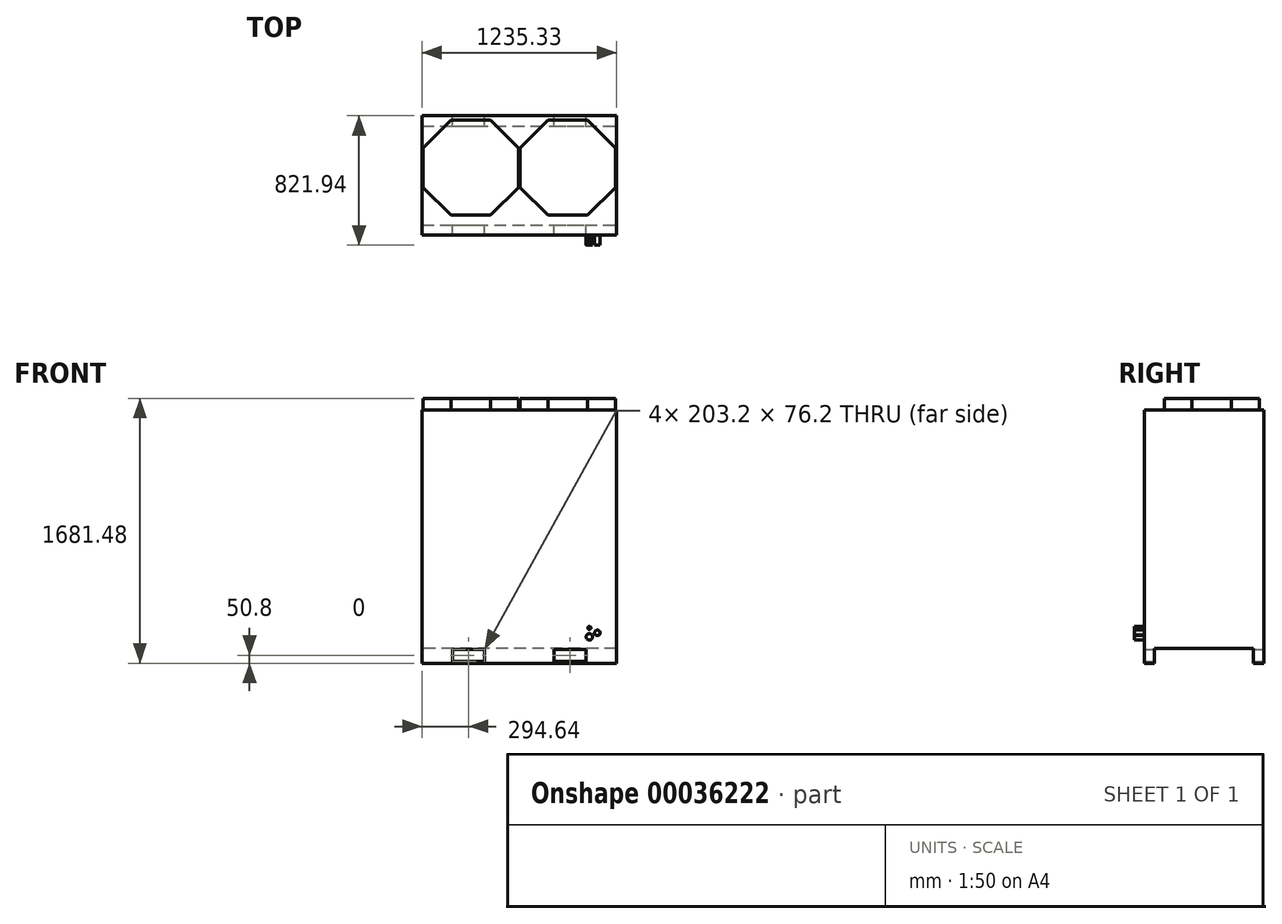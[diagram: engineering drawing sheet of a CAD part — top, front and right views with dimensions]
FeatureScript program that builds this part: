
annotation { "Feature Type Name" : "Feature", "Feature Type Description" : "" }
export const myFeature = defineFeature(function(context is Context, id is Id, definition is map)
    precondition{}
    {
        {
            var Q0;
            Q0=qCreatedBy(makeId("Front.planeOp"),FACE);
            var sketch = newSketch(context, id + "F0", { "sketchPlane" : qUnion([Q0])});
            skLineSegment(sketch, "E0.bottom", {"start": v(0, 0) * mm, "end": v(1235.33, 0) * mm});
            skLineSegment(sketch, "E0.top", {"start": v(0, 1610.36) * mm, "end": v(1235.33, 1610.36) * mm});
            skLineSegment(sketch, "E0.left", {"start": v(0, 0) * mm, "end": v(0, 1610.36) * mm});
            skLineSegment(sketch, "E0.right", {"start": v(1235.33, 0) * mm, "end": v(1235.33, 1610.36) * mm});
            skLineSegment(sketch, "E1.bottom", {"start": v(193.04, 88.9) * mm, "end": v(396.24, 88.9) * mm});
            skLineSegment(sketch, "E1.top", {"start": v(193.04, 12.7) * mm, "end": v(396.24, 12.7) * mm});
            skLineSegment(sketch, "E1.left", {"start": v(193.04, 88.9) * mm, "end": v(193.04, 12.7) * mm});
            skLineSegment(sketch, "E1.right", {"start": v(396.24, 88.9) * mm, "end": v(396.24, 12.7) * mm});
            skLineSegment(sketch, "E2.bottom", {"start": v(839.09, 88.9) * mm, "end": v(1042.29, 88.9) * mm});
            skLineSegment(sketch, "E2.top", {"start": v(839.09, 12.7) * mm, "end": v(1042.29, 12.7) * mm});
            skLineSegment(sketch, "E2.left", {"start": v(839.09, 88.9) * mm, "end": v(839.09, 12.7) * mm});
            skLineSegment(sketch, "E2.right", {"start": v(1042.29, 88.9) * mm, "end": v(1042.29, 12.7) * mm});
            skSolve(sketch);
        }
        {
            var Q0;
            Q0=qSketchRegion(id+"F0",true);
            extrude(context, id + "F1", {"entities" : qUnion([Q0]), "depth" : 758.44 * mm});
        }
        {
            var Q0;
            Q0=makeQuery(id+"F1.opExtrude","SWEPT_FACE",FACE,{"disambiguationData":[OSD([sQuery(id+"F0.wireOp",EDGE,"E0.left")])]});
            var sketch = newSketch(context, id + "F2", { "sketchPlane" : qUnion([Q0])});
            skLineSegment(sketch, "E3.bottom", {"start": v(64.77, -107.44) * mm, "end": v(693.67, -107.44) * mm});
            skLineSegment(sketch, "E3.top", {"start": v(64.77, 95.76) * mm, "end": v(693.67, 95.76) * mm});
            skLineSegment(sketch, "E3.left", {"start": v(64.77, -107.44) * mm, "end": v(64.77, 95.76) * mm});
            skLineSegment(sketch, "E3.right", {"start": v(693.67, -107.44) * mm, "end": v(693.67, 95.76) * mm});
            skSolve(sketch);
        }
        {
            var Q0;
            Q0=qSketchRegion(id+"F2",true);
            extrude(context, id + "F3", {"entities" : qUnion([Q0]), "operationType" : NewBodyOperationType.REMOVE, "endBound" : BoundingType.THROUGH_ALL, "oppositeDirection" : true, "depth" : 25.4 * mm});
        }
        {
            var Q0;
            Q0=makeQuery(id+"F1.opExtrude","SWEPT_FACE",FACE,{"disambiguationData":[OSD([sQuery(id+"F0.wireOp",EDGE,"E0.top")])]});
            var sketch = newSketch(context, id + "F4", { "sketchPlane" : qUnion([Q0])});
            skCircle(sketch, "E4.cCircle", {"center": v(309.88, -330.2) * mm, "radius": 302.26 * mm, "construction": true});
            skLineSegment(sketch, "E4.0", {"start": v(612.14, -455.4) * mm, "end": v(435.08, -632.46) * mm});
            skLineSegment(sketch, "E4.1", {"start": v(435.08, -632.46) * mm, "end": v(184.68, -632.46) * mm});
            skLineSegment(sketch, "E4.2", {"start": v(184.68, -632.46) * mm, "end": v(7.62, -455.4) * mm});
            skLineSegment(sketch, "E4.3", {"start": v(7.62, -455.4) * mm, "end": v(7.62, -205) * mm});
            skLineSegment(sketch, "E4.4", {"start": v(7.62, -205) * mm, "end": v(184.68, -27.94) * mm});
            skLineSegment(sketch, "E4.5", {"start": v(184.68, -27.94) * mm, "end": v(435.08, -27.94) * mm});
            skLineSegment(sketch, "E4.6", {"start": v(435.08, -27.94) * mm, "end": v(612.14, -205) * mm});
            skLineSegment(sketch, "E4.7", {"start": v(612.14, -205) * mm, "end": v(612.14, -455.4) * mm});
            skPoint(sketch, "E4.0.midPoint", {"position": v(523.61, -543.93) * mm});
            skCircle(sketch, "E5.cCircle", {"center": v(925.45, -330.2) * mm, "radius": 302.26 * mm, "construction": true});
            skLineSegment(sketch, "E5.0", {"start": v(1227.7, -455.4) * mm, "end": v(1050.65, -632.46) * mm});
            skLineSegment(sketch, "E5.1", {"start": v(1050.65, -632.46) * mm, "end": v(800.25, -632.46) * mm});
            skLineSegment(sketch, "E5.2", {"start": v(800.25, -632.46) * mm, "end": v(623.19, -455.4) * mm});
            skLineSegment(sketch, "E5.3", {"start": v(623.19, -455.4) * mm, "end": v(623.19, -205) * mm});
            skLineSegment(sketch, "E5.4", {"start": v(623.19, -205) * mm, "end": v(800.25, -27.94) * mm});
            skLineSegment(sketch, "E5.5", {"start": v(800.25, -27.94) * mm, "end": v(1050.65, -27.94) * mm});
            skLineSegment(sketch, "E5.6", {"start": v(1050.65, -27.94) * mm, "end": v(1227.7, -205) * mm});
            skLineSegment(sketch, "E5.7", {"start": v(1227.7, -205) * mm, "end": v(1227.7, -455.4) * mm});
            skPoint(sketch, "E5.0.midPoint", {"position": v(1139.18, -543.93) * mm});
            skSolve(sketch);
        }
        {
            var Q0;
            Q0=qSketchRegion(id+"F4",true);
            extrude(context, id + "F5", {"entities" : qUnion([Q0]), "operationType" : NewBodyOperationType.ADD, "depth" : 71.12 * mm});
        }
        {
            var Q0;
            Q0=makeQuery(id+"F1.opExtrude","CAP_FACE",FACE,{"disambiguationData":[OSD([sQuery(id+"F0.wireOp",EDGE,"E0.bottom"),sQuery(id+"F0.wireOp",EDGE,"E0.top"),sQuery(id+"F0.wireOp",EDGE,"E0.left"),sQuery(id+"F0.wireOp",EDGE,"E0.right"),sQuery(id+"F0.wireOp",EDGE,"E1.bottom"),sQuery(id+"F0.wireOp",EDGE,"E1.top"),sQuery(id+"F0.wireOp",EDGE,"E1.left"),sQuery(id+"F0.wireOp",EDGE,"E1.right"),sQuery(id+"F0.wireOp",EDGE,"E2.bottom"),sQuery(id+"F0.wireOp",EDGE,"E2.top"),sQuery(id+"F0.wireOp",EDGE,"E2.left"),sQuery(id+"F0.wireOp",EDGE,"E2.right")])],"isStart":false});
            var sketch = newSketch(context, id + "F6", { "sketchPlane" : qUnion([Q0])});
            skCircle(sketch, "E6", {"center": v(1063, 224.8) * mm, "radius": 9.53 * mm});
            skCircle(sketch, "E7", {"center": v(1113.8, 193.04) * mm, "radius": 17.46 * mm});
            skCircle(sketch, "E8", {"center": v(1063, 167.64) * mm, "radius": 20.64 * mm});
            skSolve(sketch);
        }
        {
            var Q0;
            Q0 = qSketchRegion(id + "F6", true);
            extrude(context, id + "F7", {"entities" : qUnion([Q0]), "operationType" : NewBodyOperationType.ADD, "depth" : 63.5 * mm});
        }
    });
